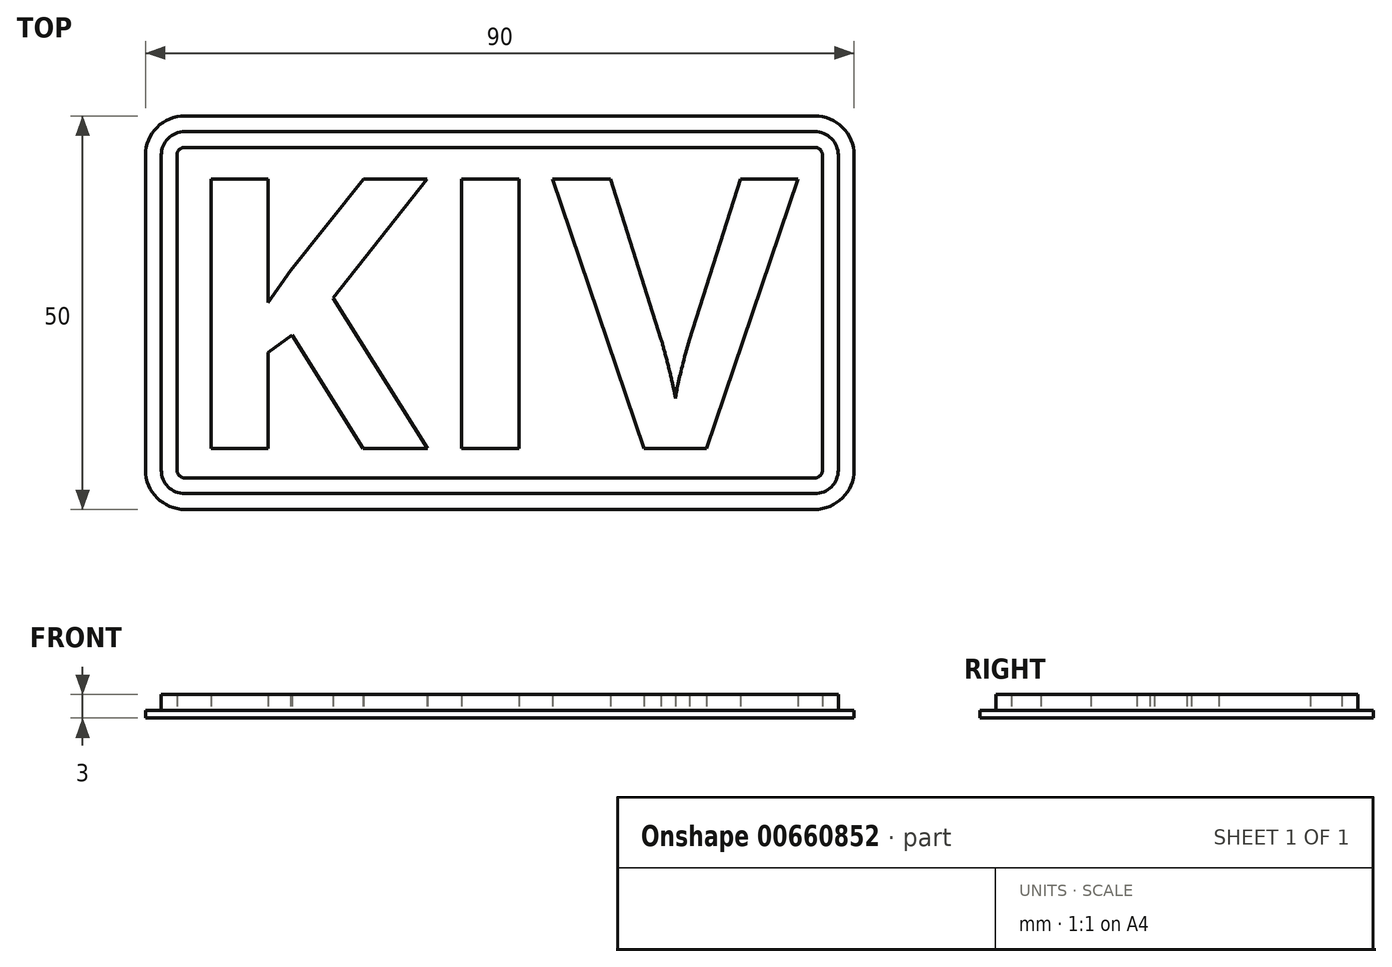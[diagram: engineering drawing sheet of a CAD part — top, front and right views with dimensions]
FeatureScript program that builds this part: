
annotation { "Feature Type Name" : "Feature", "Feature Type Description" : "" }
export const myFeature = defineFeature(function(context is Context, id is Id, definition is map)
    precondition{}
    {
        {
            assignVariable(context, id + "F0", {"variableType" : VariableType.LENGTH, "name" : "st", "lengthValue" : 1 * mm});
        }
        {
            assignVariable(context, id + "F1", {"variableType" : VariableType.LENGTH, "name" : "ft", "lengthValue" : 2 * mm});
        }
        {
            var Q0;
            Q0=qCreatedBy(makeId("Top.planeOp"),FACE);
            var sketch = newSketch(context, id + "F2", { "sketchPlane" : qUnion([Q0])});
            skLineSegment(sketch, "E0.bottom", {"start": v(-40, 25) * mm, "end": v(40, 25) * mm});
            skLineSegment(sketch, "E0.top", {"start": v(-40, -25) * mm, "end": v(40, -25) * mm});
            skLineSegment(sketch, "E0.left", {"start": v(-45, 20) * mm, "end": v(-45, -20) * mm});
            skLineSegment(sketch, "E0.right", {"start": v(45, 20) * mm, "end": v(45, -20) * mm});
            skPoint(sketch, "E1", {"position": v(0, 25) * mm});
            skPoint(sketch, "E2", {"position": v(-45, 0) * mm});
            skPoint(sketch, "E3.visualSharp", {"position": v(-45, 25) * mm});
            skArc(sketch, "E3.filletArc", {"start": v(-40, 25) * mm, "mid": v(-43.54, 23.54) * mm, "end": v(-45, 20) * mm});
            skPoint(sketch, "E4.visualSharp", {"position": v(45, 25) * mm});
            skArc(sketch, "E4.filletArc", {"start": v(45, 20) * mm, "mid": v(43.54, 23.54) * mm, "end": v(40, 25) * mm});
            skPoint(sketch, "E5.visualSharp", {"position": v(45, -25) * mm});
            skArc(sketch, "E5.filletArc", {"start": v(40, -25) * mm, "mid": v(43.54, -23.54) * mm, "end": v(45, -20) * mm});
            skPoint(sketch, "E6.visualSharp", {"position": v(-45, -25) * mm});
            skArc(sketch, "E6.filletArc", {"start": v(-45, -20) * mm, "mid": v(-43.54, -23.54) * mm, "end": v(-40, -25) * mm});
            skSolve(sketch);
        }
        {
            var Q0;
            Q0=qSketchRegion(id+"F2",true);
            extrude(context, id + "F3", {"entities" : qUnion([Q0]), "depth" : getVariable(context, 'st'), "offsetDistance" : 25 * mm});
        }
        {
            var Q0;
            Q0=makeQuery(id+"F3.opExtrude","CAP_FACE",FACE,{"disambiguationData":[OSD([sQuery(id+"F2.wireOp",EDGE,"E0.bottom"),sQuery(id+"F2.wireOp",EDGE,"E0.top"),sQuery(id+"F2.wireOp",EDGE,"E0.left"),sQuery(id+"F2.wireOp",EDGE,"E0.right"),sQuery(id+"F2.wireOp",EDGE,"E3.filletArc"),sQuery(id+"F2.wireOp",EDGE,"E4.filletArc"),sQuery(id+"F2.wireOp",EDGE,"E5.filletArc"),sQuery(id+"F2.wireOp",EDGE,"E6.filletArc")])],"isStart":false});
            var sketch = newSketch(context, id + "F4", { "sketchPlane" : qUnion([Q0])});
            skArc(sketch, "E7.0", {"start": v(-40, 23) * mm, "mid": v(-42.12, 22.12) * mm, "end": v(-43, 20) * mm});
            skLineSegment(sketch, "E7.1", {"start": v(-40, 23) * mm, "end": v(40, 23) * mm});
            skLineSegment(sketch, "E7.2", {"start": v(-43, 20) * mm, "end": v(-43, -20) * mm});
            skArc(sketch, "E7.3", {"start": v(43, 20) * mm, "mid": v(42.12, 22.12) * mm, "end": v(40, 23) * mm});
            skArc(sketch, "E7.4", {"start": v(-43, -20) * mm, "mid": v(-42.12, -22.12) * mm, "end": v(-40, -23) * mm});
            skLineSegment(sketch, "E7.5", {"start": v(-40, -23) * mm, "end": v(40, -23) * mm});
            skArc(sketch, "E7.6", {"start": v(40, -23) * mm, "mid": v(42.12, -22.12) * mm, "end": v(43, -20) * mm});
            skLineSegment(sketch, "E7.7", {"start": v(43, 20) * mm, "end": v(43, -20) * mm});
            skArc(sketch, "E8.0", {"start": v(-40, 21) * mm, "mid": v(-40.7, 20.7) * mm, "end": v(-41, 20) * mm});
            skLineSegment(sketch, "E8.1", {"start": v(-40, 21) * mm, "end": v(40, 21) * mm});
            skLineSegment(sketch, "E8.2", {"start": v(-41, 20) * mm, "end": v(-41, -20) * mm});
            skArc(sketch, "E8.3", {"start": v(41, 20) * mm, "mid": v(40.7, 20.7) * mm, "end": v(40, 21) * mm});
            skArc(sketch, "E8.4", {"start": v(-41, -20) * mm, "mid": v(-40.7, -20.7) * mm, "end": v(-40, -21) * mm});
            skLineSegment(sketch, "E8.5", {"start": v(-40, -21) * mm, "end": v(40, -21) * mm});
            skArc(sketch, "E8.6", {"start": v(40, -21) * mm, "mid": v(40.7, -20.7) * mm, "end": v(41, -20) * mm});
            skLineSegment(sketch, "E8.7", {"start": v(41, 20) * mm, "end": v(41, -20) * mm});
            skText(sketch, "E9", { "text": "KIV", "fontName": "OpenSans-Bold.ttf"});
            const initialGuessF4  = {"E9": [-0.041, -0.01726, 1, 0, 0.03453]};
            skSetInitialGuess(sketch, initialGuessF4);
            skSolve(sketch);
        }
        {
            var Q0;
            {var subQ5=sQuery(id+"F4.wireOp",EDGE,"E9.sketch_text.stroke-2");Q0=makeQuery(id+"F4.imprint","IMPRINT",FACE,{"disambiguationData":[TD([[makeQuery(id+"F4.imprint","IMPRINT",EDGE,{"derivedFrom":subQ5}),-1.0]])]});}
            var Q1;
            Q1=makeQuery(id+"F4.imprint","IMPRINT",FACE,{"disambiguationData":[TD([[makeQuery(id+"F4.imprint","IMPRINT",EDGE,{"derivedFrom":sQuery(id+"F4.wireOp",EDGE,"E7.0")}),1.0]])]});
            var Q2;
            {var subQ5=sQuery(id+"F4.wireOp",EDGE,"E9.sketch_text.stroke-14");Q2=makeQuery(id+"F4.imprint","IMPRINT",FACE,{"disambiguationData":[TD([[makeQuery(id+"F4.imprint","IMPRINT",EDGE,{"derivedFrom":subQ5}),-1.0]])]});}
            var Q3;
            {var subQ1=sQuery(id+"F4.wireOp",EDGE,"E9.sketch_text.stroke-17");Q3=makeQuery(id+"F4.imprint","IMPRINT",FACE,{"disambiguationData":[TD([[makeQuery(id+"F4.imprint","IMPRINT",EDGE,{"derivedFrom":subQ1}),-1.0]])]});}
            extrude(context, id + "F5", {"entities" : qUnion([Q0, Q1, Q2, Q3]), "operationType" : NewBodyOperationType.ADD, "depth" : getVariable(context, 'ft'), "offsetDistance" : 25 * mm});
        }
    });
